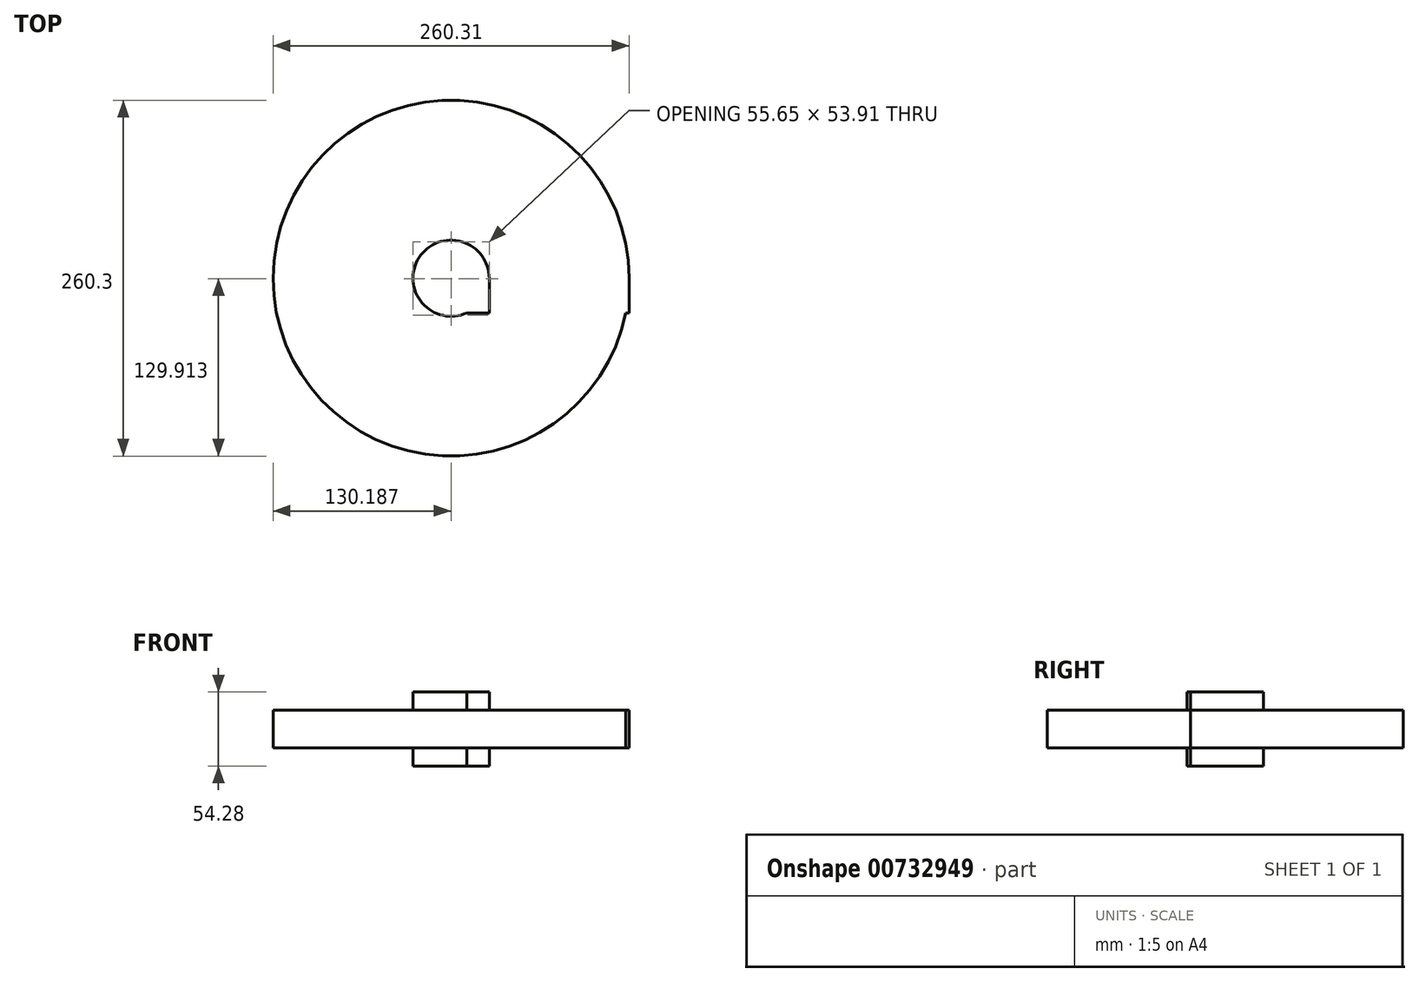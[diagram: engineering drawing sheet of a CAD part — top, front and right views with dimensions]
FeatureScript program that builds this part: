
annotation { "Feature Type Name" : "Feature", "Feature Type Description" : "" }
export const myFeature = defineFeature(function(context is Context, id is Id, definition is map)
    precondition{}
    {
        {
            var Q0;
            Q0=qCreatedBy(makeId("Front.planeOp"),FACE);
            var sketch = newSketch(context, id + "F0", { "sketchPlane" : qUnion([Q0])});
            skPoint(sketch, "E0.middle", {"position": v(0, 0) * mm});
            skLineSegment(sketch, "E1.bottom", {"start": v(51.15, 13.69) * mm, "end": v(-51.15, 13.69) * mm});
            skLineSegment(sketch, "E1.top", {"start": v(51.15, -13.69) * mm, "end": v(-51.15, -13.69) * mm});
            skLineSegment(sketch, "E1.left", {"start": v(51.15, 13.69) * mm, "end": v(51.15, -13.69) * mm});
            skLineSegment(sketch, "E1.right", {"start": v(-51.15, 13.69) * mm, "end": v(-51.15, -13.69) * mm});
            skLineSegment(sketch, "E2.bottom", {"start": v(-51.15, -27.14) * mm, "end": v(-79, -27.14) * mm});
            skLineSegment(sketch, "E2.top", {"start": v(-51.15, 27.14) * mm, "end": v(-79, 27.14) * mm});
            skLineSegment(sketch, "E2.left", {"start": v(-51.15, -27.14) * mm, "end": v(-51.15, 27.14) * mm});
            skLineSegment(sketch, "E2.right", {"start": v(-79, -27.14) * mm, "end": v(-79, 27.14) * mm});
            skPoint(sketch, "E2.middle", {"position": v(-65.08, 0) * mm});
            skSolve(sketch);
        }
        {
            var Q0;
            Q0 = qSketchRegion(id + "F0", true);
            extrude(context, id + "F1", {"entities" : qUnion([Q0]), "depth" : 25.4 * mm, "offsetDistance" : 25.4 * mm});
        }
        {
            var Q0;
            Q0=makeQuery(id+"F1.opExtrude","CAP_FACE",FACE,{"disambiguationData":[OSD([sQuery(id+"F0.wireOp",EDGE,"E1.bottom"),sQuery(id+"F0.wireOp",EDGE,"E1.top"),sQuery(id+"F0.wireOp",EDGE,"E1.left"),sQuery(id+"F0.wireOp",EDGE,"E2.bottom"),sQuery(id+"F0.wireOp",EDGE,"E2.top"),sQuery(id+"F0.wireOp",EDGE,"E2.left"),sQuery(id+"F0.wireOp",EDGE,"E2.right")])],"isStart":true});
            var Q1;
            Q1=makeQuery(id+"F1.opExtrude","SWEPT_FACE",FACE,{"disambiguationData":[OSD([sQuery(id+"F0.wireOp",EDGE,"E2.right")])]});
            var Q2;
            Q2=makeQuery(id+"F1.opExtrude","CAP_EDGE",EDGE,{"disambiguationData":[OSD([sQuery(id+"F0.wireOp",EDGE,"E2.right")])],"isStart":true});
            revolve(context, id + "F2", {"operationType" : NewBodyOperationType.ADD, "surfaceOperationType" : NewSurfaceOperationType.NEW, "entities" : qUnion([Q0, Q1]), "axis" : qUnion([Q2]), "revolveType" : RevolveType.FULL});
        }
    });
